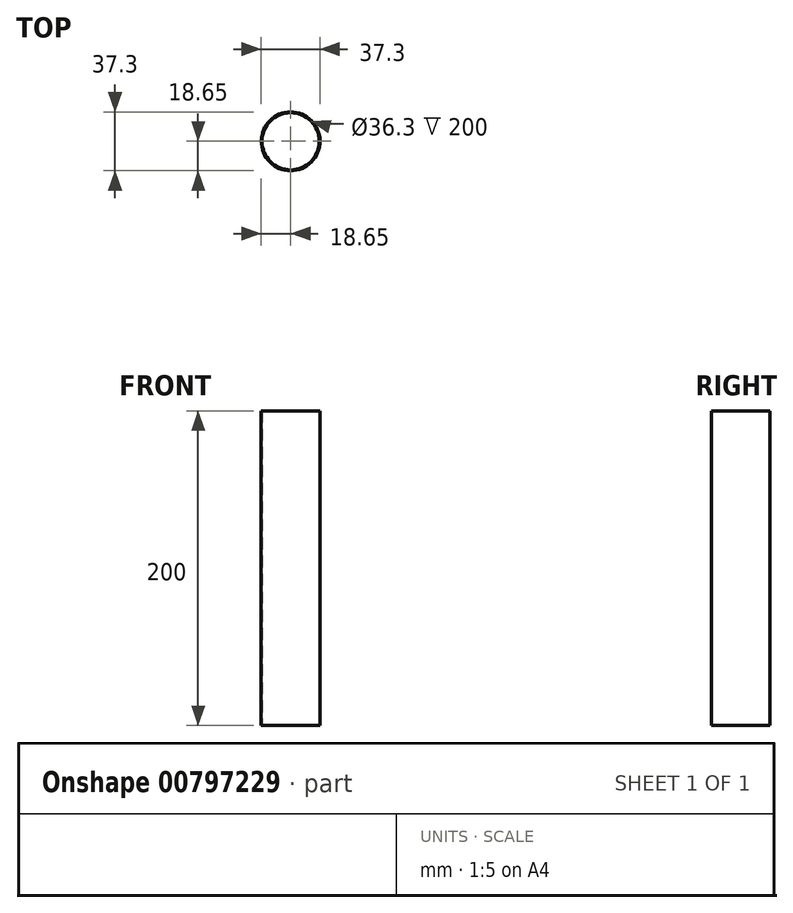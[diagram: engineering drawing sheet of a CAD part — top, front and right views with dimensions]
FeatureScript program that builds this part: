
annotation { "Feature Type Name" : "Feature", "Feature Type Description" : "" }
export const myFeature = defineFeature(function(context is Context, id is Id, definition is map)
    precondition{}
    {
        {
            var Q0;
            Q0=qCreatedBy(makeId("Top.planeOp"),FACE);
            var sketch = newSketch(context, id + "F0", { "sketchPlane" : qUnion([Q0])});
            skCircle(sketch, "E0", {"center": v(0, 0) * mm, "radius": 18.65 * mm});
            skCircle(sketch, "E1", {"center": v(0, 0) * mm, "radius": 18.15 * mm});
            skSolve(sketch);
        }
        {
            var Q0;
            Q0 = qSketchRegion(id + "F0", true);
            extrude(context, id + "F1", {"entities" : qUnion([Q0]), "depth" : 200 * mm, "offsetDistance" : 25 * mm});
        }
    });
